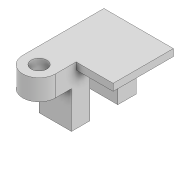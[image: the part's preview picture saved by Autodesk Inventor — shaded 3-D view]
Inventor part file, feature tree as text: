
AUTODESK INVENTOR PART (.ipt)
format: ipt  version: 2022 (Build 260153000, 153)  size: 125,440 bytes
history: native  units: mm
features: sketch x4, extrude x3, hole x1, projected_geometry x1
ambient origin geometry x8: Origin, YZ Plane, XZ Plane, XY Plane, X Axis, Y Axis, Z Axis, Center Point
bodies: Solid1 (feature_tree)
feature tree (9):
  extrude  "Extrusion1"  Depth=15.0mm
  extrude  "Extrusion2"  Depth=8.0mm
  extrude  "Extrusion3"  Depth=1.5mm TaperAngle=0.0deg
  hole  "Hole1"  [1 undecoded]
  sketch  "Sketch1"  dims[d0=13.0mm d1=15.0mm]
  sketch  "Sketch2"  dims[d3=7.0mm d4=8.0mm]
  projected_geometry  "Projected Loop1"
  sketch  "Sketch3"  dims[d5=8.0mm d6=1.5mm d7=0.0mm]
  sketch  "Sketch4"  dims[d8=3.0mm d9=0.0mm d10=4.0mm d11=8.0mm d12=1.0mm d13=4.0mm d14=3.0mm d15=0.0mm d16=3.4mm d17=6.0mm d18=4.0mm d19=2.0mm d20=90.0deg d21=8.0mm d22=20.594885mm]
note: 1 required parameter value undecoded (feature->parameter linkage not recoverable at this tier; creation-order binding heuristic only, values carry confidence <= 0.55)
